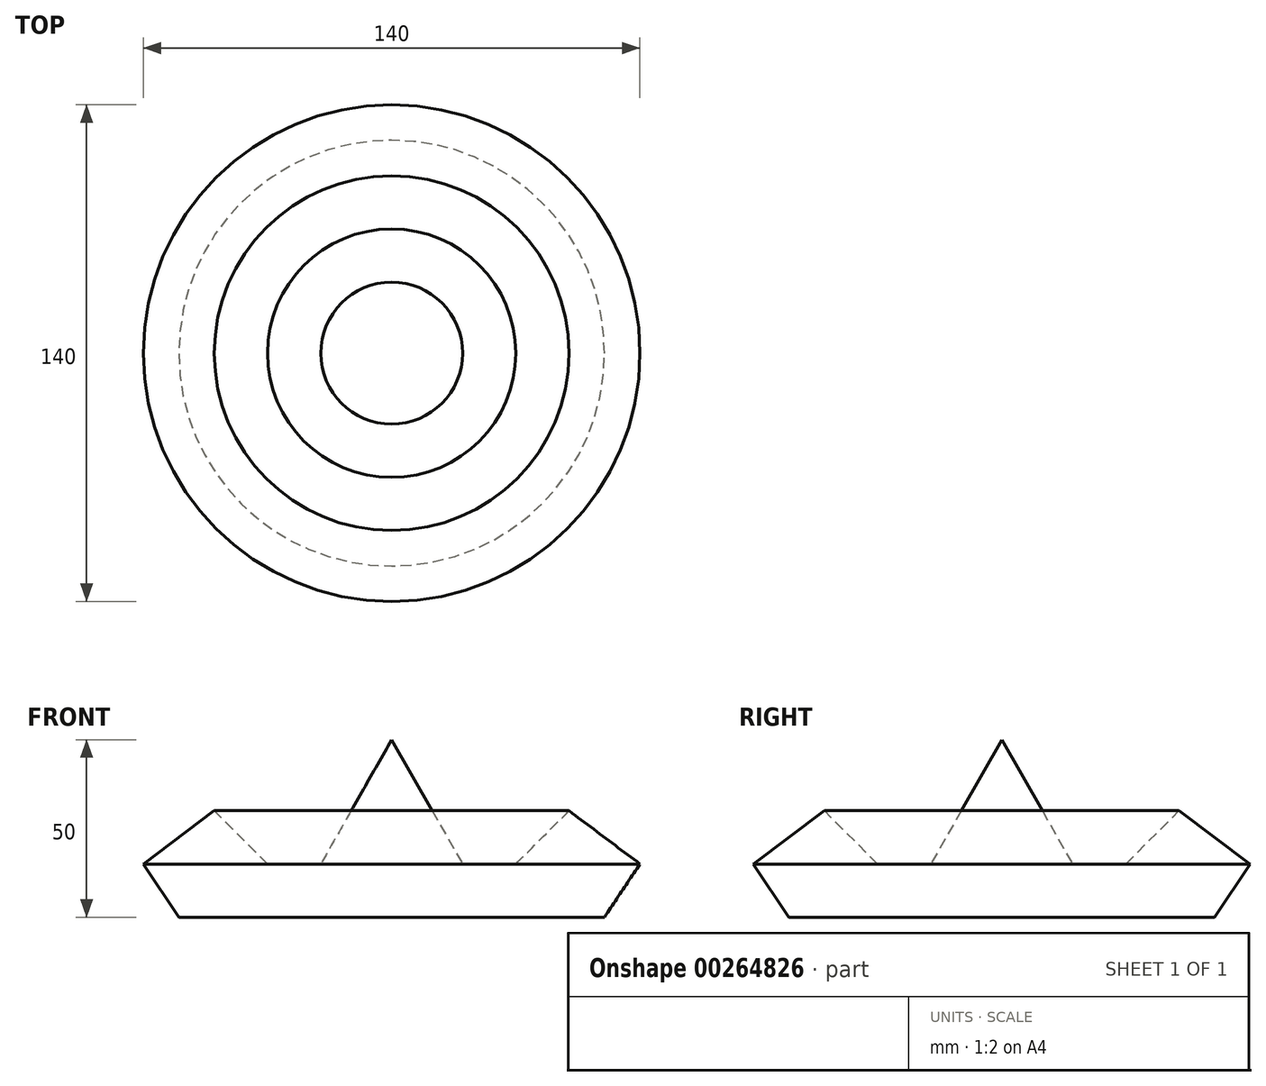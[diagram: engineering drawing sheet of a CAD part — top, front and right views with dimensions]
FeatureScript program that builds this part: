
annotation { "Feature Type Name" : "Feature", "Feature Type Description" : "" }
export const myFeature = defineFeature(function(context is Context, id is Id, definition is map)
    precondition{}
    {
        {
            var Q0;
            Q0=qCreatedBy(makeId("Top.planeOp"),FACE);
            var sketch = newSketch(context, id + "F0", { "sketchPlane" : qUnion([Q0])});
            skCircle(sketch, "E0", {"center": v(0, 0) * mm, "radius": 70 * mm});
            skLineSegment(sketch, "E1", {"start": v(-70, 0) * mm, "end": v(70, 0) * mm, "construction": true});
            skSolve(sketch);
        }
        {
            var Q0;
            Q0=qCreatedBy(makeId("Top.planeOp"),FACE);
            cPlane(context, id + "F1", {"entities" : qUnion([Q0]), "cplaneType" : CPlaneType.OFFSET, "offset" : 15 * mm, "width" : 150 * mm, "height" : 150 * mm});
        }
        {
            var Q0;
            Q0=qCreatedBy(id+"F1.planeOp",FACE);
            var sketch = newSketch(context, id + "F2", { "sketchPlane" : qUnion([Q0])});
            skCircle(sketch, "E2", {"center": v(0, 0) * mm, "radius": 50 * mm});
            skLineSegment(sketch, "E3", {"start": v(-50, 0) * mm, "end": v(50, 0) * mm, "construction": true});
            skSolve(sketch);
        }
        {
            var Q0;
            Q0=makeQuery(id+"F0.imprint","IMPRINT",FACE,{"disambiguationData":[TD([[makeQuery(id+"F0.imprint","IMPRINT",EDGE,{"derivedFrom":sQuery(id+"F0.wireOp",EDGE,"E0")}),1.0]])]});
            var Q1;
            Q1=makeQuery(id+"F2.imprint","IMPRINT",FACE,{"disambiguationData":[TD([[makeQuery(id+"F2.imprint","IMPRINT",EDGE,{"derivedFrom":sQuery(id+"F2.wireOp",EDGE,"E2")}),1.0]])]});
            loft(context, id + "F3", {"sheetProfilesArray" : [{ "sheetProfileEntities" : qUnion([Q0]) }, { "sheetProfileEntities" : qUnion([Q1]) }]});
        }
        {
            var Q0;
            Q0=qCreatedBy(makeId("Top.planeOp"),FACE);
            cPlane(context, id + "F4", {"entities" : qUnion([Q0]), "cplaneType" : CPlaneType.OFFSET, "offset" : 15 * mm, "oppositeDirection" : true, "width" : 150 * mm, "height" : 150 * mm});
        }
        {
            var Q0;
            Q0=qCreatedBy(id+"F4.planeOp",FACE);
            var sketch = newSketch(context, id + "F5", { "sketchPlane" : qUnion([Q0])});
            skCircle(sketch, "E4", {"center": v(0, 0) * mm, "radius": 60 * mm});
            skLineSegment(sketch, "E5", {"start": v(-60, 0) * mm, "end": v(60, 0) * mm, "construction": true});
            skSolve(sketch);
        }
        {
            var Q1;
            Q1=makeQuery(id+"F5.imprint","IMPRINT",FACE,{"disambiguationData":[TD([[makeQuery(id+"F5.imprint","IMPRINT",EDGE,{"derivedFrom":sQuery(id+"F5.wireOp",EDGE,"E4")}),1.0]])]});
            var Q2;
            Q2=makeQuery(id+"F3.opLoft","CAP_FACE",FACE,{"disambiguationData":[OSD([makeQuery(id+"F0.imprint","IMPRINT",FACE,{"disambiguationData":[TD([[makeQuery(id+"F0.imprint","IMPRINT",EDGE,{"derivedFrom":sQuery(id+"F0.wireOp",EDGE,"E0")}),1.0]])]})])],"isStart":true});
            loft(context, id + "F6", {"sheetProfilesArray" : [{ "sheetProfileEntities" : qUnion([Q1]) }, { "sheetProfileEntities" : qUnion([Q2]) }]});
        }
        {
            var Q0;
            Q0=qCreatedBy(makeId("Top.planeOp"),FACE);
            var sketch = newSketch(context, id + "F7", { "sketchPlane" : qUnion([Q0])});
            skCircle(sketch, "E6", {"center": v(0, 0) * mm, "radius": 35 * mm});
            skLineSegment(sketch, "E7", {"start": v(-35, 0) * mm, "end": v(35, 0) * mm, "construction": true});
            skSolve(sketch);
        }
        {
            var Q1;
            Q1=makeQuery(id+"F3.opLoft","CAP_FACE",FACE,{"disambiguationData":[OSD([makeQuery(id+"F2.imprint","IMPRINT",FACE,{"disambiguationData":[TD([[makeQuery(id+"F2.imprint","IMPRINT",EDGE,{"derivedFrom":sQuery(id+"F2.wireOp",EDGE,"E2")}),1.0]])]})])],"isStart":true});
            var Q2;
            Q2 = qSketchRegion(id + "F7", true);
            loft(context, id + "F8", {"operationType" : NewBodyOperationType.REMOVE, "sheetProfilesArray" : [{ "sheetProfileEntities" : qUnion([Q1]) }, { "sheetProfileEntities" : qUnion([Q2]) }]});
        }
        {
            var Q0;
            Q0=qCreatedBy(makeId("Top.planeOp"),FACE);
            var sketch = newSketch(context, id + "F9", { "sketchPlane" : qUnion([Q0])});
            skCircle(sketch, "E8", {"center": v(0, 0) * mm, "radius": 20 * mm});
            skLineSegment(sketch, "E9", {"start": v(-20, 0) * mm, "end": v(20, 0) * mm, "construction": true});
            skSolve(sketch);
        }
        {
            var Q0;
            Q0=qCreatedBy(id+"F1.planeOp",FACE);
            cPlane(context, id + "F10", {"entities" : qUnion([Q0]), "cplaneType" : CPlaneType.OFFSET, "offset" : 20 * mm, "width" : 150 * mm, "height" : 150 * mm});
        }
        {
            var Q0;
            Q0=qCreatedBy(id+"F10.planeOp",FACE);
            var sketch = newSketch(context, id + "F11", { "sketchPlane" : qUnion([Q0])});
            skPoint(sketch, "E10", {"position": v(0, 0) * mm});
            skSolve(sketch);
        }
        {
            var Q1;
            Q1=makeQuery(id+"F9.imprint","IMPRINT",FACE,{"disambiguationData":[TD([[makeQuery(id+"F9.imprint","IMPRINT",EDGE,{"derivedFrom":sQuery(id+"F9.wireOp",EDGE,"E8")}),1.0]])]});
            var Q2;
            Q2=sQuery(id+"F11.wireOp",VERTEX,"E10");
            loft(context, id + "F12", {"sheetProfilesArray" : [{ "sheetProfileEntities" : qUnion([Q1]) }, { "sheetProfileEntities" : qUnion([Q2]) }]});
        }
    });
